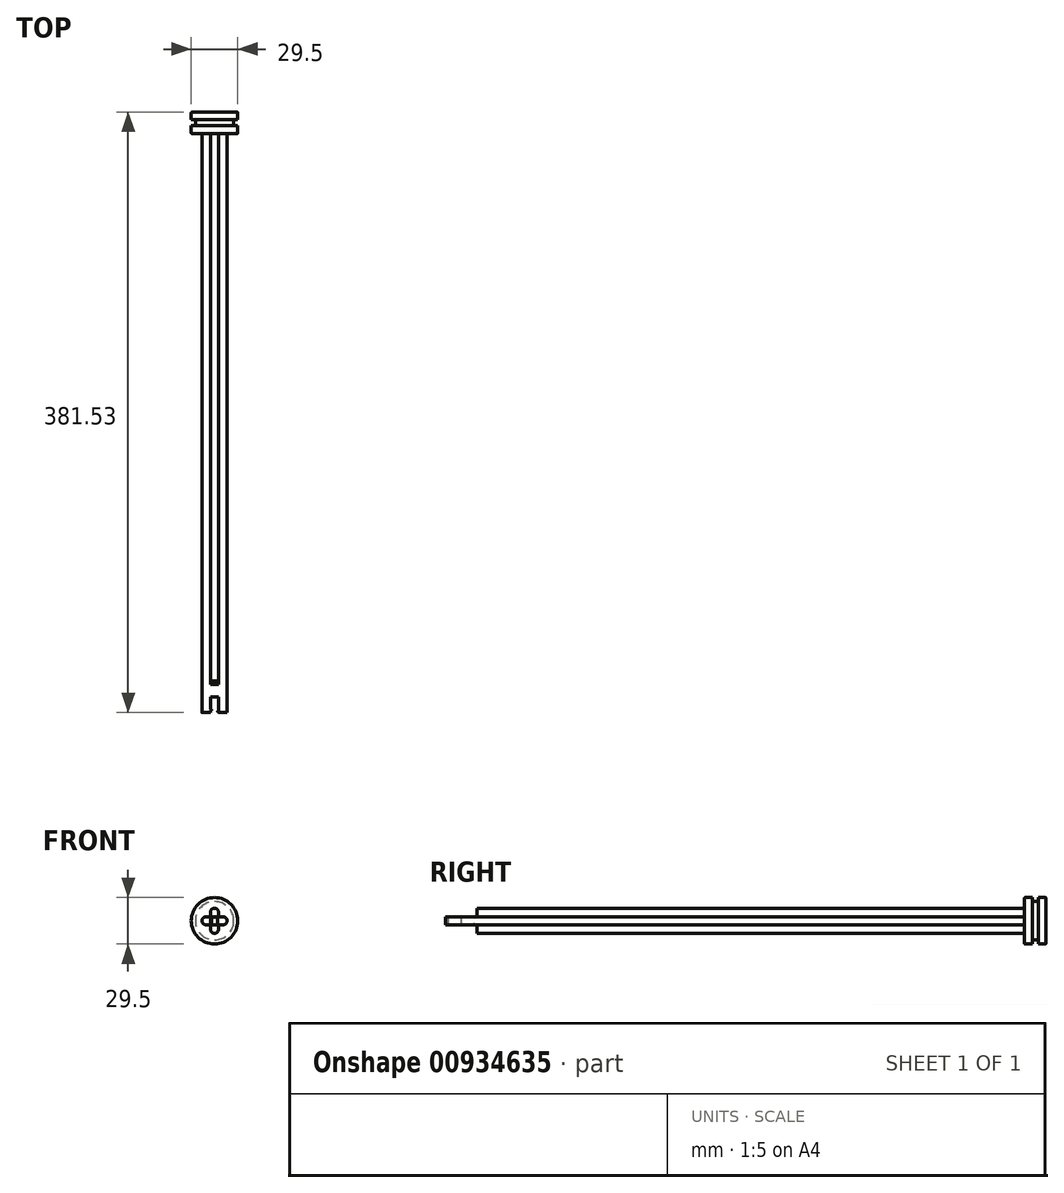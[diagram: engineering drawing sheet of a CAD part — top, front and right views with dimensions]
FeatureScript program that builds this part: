
annotation { "Feature Type Name" : "Feature", "Feature Type Description" : "" }
export const myFeature = defineFeature(function(context is Context, id is Id, definition is map)
    precondition{}
    {
        {
            var Q0;
            Q0=qCreatedBy(makeId("Front.planeOp"),FACE);
            var sketch = newSketch(context, id + "F0", { "sketchPlane" : qUnion([Q0])});
            skLineSegment(sketch, "E0.bottom", {"start": v(2.5, 8) * mm, "end": v(-2.5, 8) * mm});
            skLineSegment(sketch, "E0.top", {"start": v(2.5, -8) * mm, "end": v(-2.5, -8) * mm});
            skLineSegment(sketch, "E0.left", {"start": v(2.5, 8) * mm, "end": v(2.5, -8) * mm});
            skLineSegment(sketch, "E0.right", {"start": v(-2.5, 8) * mm, "end": v(-2.5, -8) * mm});
            skPoint(sketch, "E0.middle", {"position": v(0, 0) * mm});
            skLineSegment(sketch, "E1.bottom", {"start": v(-8, -2.5) * mm, "end": v(8, -2.5) * mm});
            skLineSegment(sketch, "E1.top", {"start": v(-8, 2.5) * mm, "end": v(8, 2.5) * mm});
            skLineSegment(sketch, "E1.left", {"start": v(-8, -2.5) * mm, "end": v(-8, 2.5) * mm});
            skLineSegment(sketch, "E1.right", {"start": v(8, -2.5) * mm, "end": v(8, 2.5) * mm});
            skSolve(sketch);
        }
        {
            var Q0;
            {var subQ5=sQuery(id+"F0.wireOp",EDGE,"E1.left");Q0=makeQuery(id+"F0.imprint","IMPRINT",FACE,{"disambiguationData":[TD([[makeQuery(id+"F0.imprint","IMPRINT",EDGE,{"derivedFrom":subQ5}),-1.0]])]});}
            var Q1;
            {var subQ0=sQuery(id+"F0.wireOp",EDGE,"E1.top");var subQ1=sQuery(id+"F0.wireOp",EDGE,"E0.left");var subQ2=makeQuery(id+"F0.imprint","INTERSECT",VERTEX,{"derivedFrom":[subQ1,subQ0]});Q1=makeQuery(id+"F0.imprint","IMPRINT",FACE,{"disambiguationData":[TD([[makeQuery(id+"F0.imprint","IMPRINT",EDGE,{"disambiguationData":[TD([[subQ2,-1.0]])],"derivedFrom":subQ1}),-1.0]])]});}
            var Q2;
            {var subQ5=sQuery(id+"F0.wireOp",EDGE,"E1.right");Q2=makeQuery(id+"F0.imprint","IMPRINT",FACE,{"disambiguationData":[TD([[makeQuery(id+"F0.imprint","IMPRINT",EDGE,{"derivedFrom":subQ5}),1.0]])]});}
            var Q3;
            {var subQ0=sQuery(id+"F0.wireOp",EDGE,"E0.top");Q3=makeQuery(id+"F0.imprint","IMPRINT",FACE,{"disambiguationData":[TD([[makeQuery(id+"F0.imprint","IMPRINT",EDGE,{"derivedFrom":subQ0}),-1.0]])]});}
            var Q4;
            {var subQ0=sQuery(id+"F0.wireOp",EDGE,"E0.bottom");Q4=makeQuery(id+"F0.imprint","IMPRINT",FACE,{"disambiguationData":[TD([[makeQuery(id+"F0.imprint","IMPRINT",EDGE,{"derivedFrom":subQ0}),1.0]])]});}
            extrude(context, id + "F1", {"entities" : qUnion([Q0, Q1, Q2, Q3, Q4]), "depth" : 367.74 * mm, "offsetDistance" : 25.4 * mm});
        }
        {
            var Q0;
            Q0=makeQuery(id+"F1.opExtrude","SWEPT_EDGE",EDGE,{"disambiguationData":[OSD([sQuery(id+"F0.wireOp",EDGE,"E0.bottom"),sQuery(id+"F0.wireOp",EDGE,"E0.right")])]});
            var Q1;
            Q1=makeQuery(id+"F1.opExtrude","SWEPT_EDGE",EDGE,{"disambiguationData":[OSD([sQuery(id+"F0.wireOp",EDGE,"E0.bottom"),sQuery(id+"F0.wireOp",EDGE,"E0.left")])]});
            var Q2;
            Q2=makeQuery(id+"F1.opExtrude","SWEPT_EDGE",EDGE,{"disambiguationData":[OSD([sQuery(id+"F0.wireOp",EDGE,"E1.top"),sQuery(id+"F0.wireOp",EDGE,"E1.left")])]});
            var Q3;
            Q3=makeQuery(id+"F1.opExtrude","SWEPT_EDGE",EDGE,{"disambiguationData":[OSD([sQuery(id+"F0.wireOp",EDGE,"E1.bottom"),sQuery(id+"F0.wireOp",EDGE,"E1.left")])]});
            var Q4;
            Q4=makeQuery(id+"F1.opExtrude","SWEPT_EDGE",EDGE,{"disambiguationData":[OSD([sQuery(id+"F0.wireOp",EDGE,"E0.top"),sQuery(id+"F0.wireOp",EDGE,"E0.right")])]});
            var Q5;
            Q5=makeQuery(id+"F1.opExtrude","SWEPT_EDGE",EDGE,{"disambiguationData":[OSD([sQuery(id+"F0.wireOp",EDGE,"E0.top"),sQuery(id+"F0.wireOp",EDGE,"E0.left")])]});
            var Q6;
            Q6=makeQuery(id+"F1.opExtrude","SWEPT_EDGE",EDGE,{"disambiguationData":[OSD([sQuery(id+"F0.wireOp",EDGE,"E1.bottom"),sQuery(id+"F0.wireOp",EDGE,"E1.right")])]});
            var Q7;
            Q7=makeQuery(id+"F1.opExtrude","SWEPT_EDGE",EDGE,{"disambiguationData":[OSD([sQuery(id+"F0.wireOp",EDGE,"E1.top"),sQuery(id+"F0.wireOp",EDGE,"E1.right")])]});
            fillet(context, id + "F2", {"entities" : qUnion([Q0, Q1, Q2, Q3, Q4, Q5, Q6, Q7]), "radius" : 2.5 * mm, "tangentPropagation" : true, "allowEdgeOverflow" : false});
        }
        {
            var Q0;
            Q0=qCreatedBy(makeId("Front.planeOp"),FACE);
            var sketch = newSketch(context, id + "F3", { "sketchPlane" : qUnion([Q0])});
            skCircle(sketch, "E2", {"center": v(0, 0) * mm, "radius": 14.75 * mm});
            skCircle(sketch, "E3", {"center": v(0, 0) * mm, "radius": 12.2 * mm});
            skSolve(sketch);
        }
        {
            var Q0;
            Q0=makeQuery(id+"F3.imprint","IMPRINT",FACE,{"disambiguationData":[TD([[makeQuery(id+"F3.imprint","IMPRINT",EDGE,{"derivedFrom":sQuery(id+"F3.wireOp",EDGE,"E2")}),1.0]])]});
            var Q1;
            Q1=makeQuery(id+"F3.imprint","IMPRINT",FACE,{"disambiguationData":[TD([[makeQuery(id+"F3.imprint","IMPRINT",EDGE,{"derivedFrom":sQuery(id+"F3.wireOp",EDGE,"E3")}),1.0]])]});
            extrude(context, id + "F4", {"entities" : qUnion([Q0, Q1]), "operationType" : NewBodyOperationType.ADD, "oppositeDirection" : true, "depth" : 13.8 * mm, "offsetDistance" : 25.4 * mm});
        }
        {
            var Q0;
            {var subQ0=sQuery(id+"F0.wireOp",EDGE,"E0.right");Q0=makeQuery(id+"F1.opExtrude","CAP_EDGE",EDGE,{"disambiguationData":[OSD([subQ0]),TDD([makeQuery(id+"F0.imprint","IMPRINT",EDGE,{"disambiguationData":[TD([[makeQuery(id+"F0.imprint","INTERSECT",VERTEX,{"derivedFrom":[sQuery(id+"F0.wireOp",EDGE,"E0.bottom"),subQ0]}),-1.0]])],"derivedFrom":subQ0})])],"isStart":true});}
            var Q1;
            Q1=makeQuery(id+"F4.opExtrude","CAP_FACE",FACE,{"disambiguationData":[OSD([sQuery(id+"F3.wireOp",EDGE,"E2")])],"isStart":true});
            var Q2;
            Q2=makeQuery(id+"F4.opExtrude","CAP_EDGE",EDGE,{"disambiguationData":[OSD([sQuery(id+"F3.wireOp",EDGE,"E2")])],"isStart":false});
            fillet(context, id + "F5", {"entities" : qUnion([Q0, Q1, Q2]), "radius" : 0.5 * mm, "tangentPropagation" : true, "allowEdgeOverflow" : false});
        }
        {
            var Q0;
            Q0=qCreatedBy(makeId("Right.planeOp"),FACE);
            var sketch = newSketch(context, id + "F6", { "sketchPlane" : qUnion([Q0])});
            skLineSegment(sketch, "E4.bottom", {"start": v(5, 22.2) * mm, "end": v(8.8, 22.2) * mm});
            skLineSegment(sketch, "E4.top", {"start": v(5, 12.2) * mm, "end": v(8.8, 12.2) * mm});
            skLineSegment(sketch, "E4.left", {"start": v(5, 22.2) * mm, "end": v(5, 12.2) * mm});
            skLineSegment(sketch, "E4.right", {"start": v(8.8, 22.2) * mm, "end": v(8.8, 12.2) * mm});
            skLineSegment(sketch, "E5", {"start": v(0, 0) * mm, "end": v(33.95, 0) * mm});
            skSolve(sketch);
        }
        {
            var Q0;
            Q0=makeQuery(id+"F6.imprint","IMPRINT",FACE,{"disambiguationData":[TD([[makeQuery(id+"F6.imprint","IMPRINT",EDGE,{"derivedFrom":sQuery(id+"F6.wireOp",EDGE,"E4.bottom")}),-1.0]])]});
            var Q1;
            Q1=sQuery(id+"F6.wireOp",EDGE,"E5");
            revolve(context, id + "F7", {"operationType" : NewBodyOperationType.REMOVE, "surfaceOperationType" : NewSurfaceOperationType.NEW, "entities" : qUnion([Q0]), "axis" : qUnion([Q1]), "revolveType" : RevolveType.FULL, "oppositeDirection" : true});
        }
        {
            var Q0;
            Q0=makeQuery(id+"F1.opExtrude","CAP_FACE",FACE,{"disambiguationData":[OSD([sQuery(id+"F0.wireOp",EDGE,"E0.bottom"),sQuery(id+"F0.wireOp",EDGE,"E0.top"),sQuery(id+"F0.wireOp",EDGE,"E0.left"),sQuery(id+"F0.wireOp",EDGE,"E0.right"),sQuery(id+"F0.wireOp",EDGE,"E1.bottom"),sQuery(id+"F0.wireOp",EDGE,"E1.top"),sQuery(id+"F0.wireOp",EDGE,"E1.left"),sQuery(id+"F0.wireOp",EDGE,"E1.right")])],"isStart":false});
            var sketch = newSketch(context, id + "F8", { "sketchPlane" : qUnion([Q0])});
            skLineSegment(sketch, "E6.bottom", {"start": v(2.5, 10) * mm, "end": v(-2.5, 10) * mm});
            skLineSegment(sketch, "E6.top", {"start": v(2.5, -10) * mm, "end": v(-2.5, -10) * mm});
            skLineSegment(sketch, "E6.left", {"start": v(2.5, 10) * mm, "end": v(2.5, -10) * mm});
            skLineSegment(sketch, "E6.right", {"start": v(-2.5, 10) * mm, "end": v(-2.5, -10) * mm});
            skPoint(sketch, "E6.middle", {"position": v(0, 0) * mm});
            skSolve(sketch);
        }
        {
            var Q0;
            {var subQ1=sQuery(id+"F0.wireOp",EDGE,"E1.top");var subQ2=sQuery(id+"F0.wireOp",EDGE,"E1.bottom");var subQ3=sQuery(id+"F0.wireOp",EDGE,"E0.right");var subQ4=sQuery(id+"F0.wireOp",EDGE,"E0.left");var subQ5=sQuery(id+"F0.wireOp",EDGE,"E0.top");var subQ6=sQuery(id+"F0.wireOp",EDGE,"E0.bottom");var subQ7=makeQuery(id+"F1.opExtrude","CAP_FACE",FACE,{"disambiguationData":[OSD([subQ6,subQ5,subQ4,subQ3,subQ2,subQ1,sQuery(id+"F0.wireOp",EDGE,"E1.left"),sQuery(id+"F0.wireOp",EDGE,"E1.right")])],"isStart":false});var subQ11=makeQuery(id+"F2.opFillet","BLEND_EDGE",EDGE,{"blendedFrom":[makeQuery(id+"F1.opExtrude","SWEPT_EDGE",EDGE,{"disambiguationData":[OSD([subQ6,subQ4])]}),subQ7],"blendedInto":[subQ7]});Q0=makeQuery(id+"F8.imprint","IMPRINT",FACE,{"disambiguationData":[TD([[makeQuery(id+"F8.imprint","IMPRINT",EDGE,{"derivedFrom":subQ11}),1.0]])]});}
            extrude(context, id + "F9", {"entities" : qUnion([Q0]), "operationType" : NewBodyOperationType.REMOVE, "oppositeDirection" : true, "depth" : 10 * mm, "offsetDistance" : 25 * mm});
        }
        {
            var Q0;
            Q0=makeQuery(id+"F9.boolean.opBoolean","COPY",FACE,{"derivedFrom":makeQuery(id+"F9.opExtrude","CAP_FACE",FACE,{"disambiguationData":[OSD([sQuery(id+"F0.wireOp",EDGE,"E0.bottom"),sQuery(id+"F0.wireOp",EDGE,"E0.top"),sQuery(id+"F0.wireOp",EDGE,"E0.left"),sQuery(id+"F0.wireOp",EDGE,"E0.right"),sQuery(id+"F0.wireOp",EDGE,"E1.bottom"),sQuery(id+"F0.wireOp",EDGE,"E1.top"),sQuery(id+"F0.wireOp",EDGE,"E1.left"),sQuery(id+"F0.wireOp",EDGE,"E1.right"),sQuery(id+"F8.wireOp",EDGE,"E6.left"),sQuery(id+"F8.wireOp",EDGE,"E6.right")])],"isStart":false})});
            var sketch = newSketch(context, id + "F10", { "sketchPlane" : qUnion([Q0])});
            skLineSegment(sketch, "E7.bottom", {"start": v(0, 8) * mm, "end": v(2.5, 8) * mm});
            skLineSegment(sketch, "E7.top", {"start": v(0, 2.5) * mm, "end": v(2.5, 2.5) * mm});
            skLineSegment(sketch, "E7.left", {"start": v(0, 8) * mm, "end": v(0, 2.5) * mm});
            skLineSegment(sketch, "E7.right", {"start": v(2.5, 8) * mm, "end": v(2.5, 2.5) * mm});
            skLineSegment(sketch, "E8.MirrorCS", {"start": v(0, 8) * mm, "end": v(-2.5, 8) * mm});
            skLineSegment(sketch, "E9.MirrorCS", {"start": v(-2.5, 8) * mm, "end": v(-2.5, 2.5) * mm});
            skLineSegment(sketch, "E10.MirrorCS", {"start": v(0, 2.5) * mm, "end": v(-2.5, 2.5) * mm});
            skLineSegment(sketch, "E11.bottom", {"start": v(-2.5, 8) * mm, "end": v(2.5, 8) * mm});
            skLineSegment(sketch, "E11.top", {"start": v(-2.5, 2.5) * mm, "end": v(2.5, 2.5) * mm});
            skLineSegment(sketch, "E12.MirrorCS", {"start": v(-2.5, -8) * mm, "end": v(-2.5, -2.5) * mm});
            skLineSegment(sketch, "E13.MirrorCS", {"start": v(-2.5, -8) * mm, "end": v(2.5, -8) * mm});
            skLineSegment(sketch, "E14.MirrorCS", {"start": v(2.5, -8) * mm, "end": v(2.5, -2.5) * mm});
            skLineSegment(sketch, "E15.MirrorCS", {"start": v(-2.5, -2.5) * mm, "end": v(2.5, -2.5) * mm});
            skSolve(sketch);
        }
        {
            var Q0;
            {var subQ15=sQuery(id+"F10.wireOp",EDGE,"E7.left");Q0=makeQuery(id+"F10.imprint","IMPRINT",FACE,{"disambiguationData":[TD([[makeQuery(id+"F10.imprint","IMPRINT",EDGE,{"derivedFrom":subQ15}),-1.0]])]});}
            var Q1;
            {var subQ13=sQuery(id+"F10.wireOp",EDGE,"E7.left");Q1=makeQuery(id+"F10.imprint","IMPRINT",FACE,{"disambiguationData":[TD([[makeQuery(id+"F10.imprint","IMPRINT",EDGE,{"derivedFrom":subQ13}),1.0]])]});}
            var Q2;
            {var subQ16=sQuery(id+"F10.wireOp",EDGE,"E15.MirrorCS");Q2=makeQuery(id+"F10.imprint","IMPRINT",FACE,{"disambiguationData":[TD([[makeQuery(id+"F10.imprint","IMPRINT",EDGE,{"derivedFrom":subQ16}),-1.0]])]});}
            extrude(context, id + "F11", {"entities" : qUnion([Q0, Q1, Q2]), "operationType" : NewBodyOperationType.REMOVE, "oppositeDirection" : true, "depth" : 10 * mm, "offsetDistance" : 25 * mm});
        }
        {
            var Q0;
            {var subQ0=sQuery(id+"F0.wireOp",EDGE,"E1.top");Q0=makeQuery(id+"F11.boolean.opBoolean","MERGE",FACE,{"derivedFrom":[makeQuery(id+"F1.opExtrude","SWEPT_FACE",FACE,{"disambiguationData":[OSD([subQ0]),TDD([makeQuery(id+"F0.imprint","IMPRINT",EDGE,{"disambiguationData":[TD([[makeQuery(id+"F0.imprint","INTERSECT",VERTEX,{"derivedFrom":[subQ0,sQuery(id+"F0.wireOp",EDGE,"E1.left")]}),-1.0]])],"derivedFrom":subQ0})])]}),makeQuery(id+"F1.opExtrude","SWEPT_FACE",FACE,{"disambiguationData":[OSD([subQ0]),TDD([makeQuery(id+"F0.imprint","IMPRINT",EDGE,{"disambiguationData":[TD([[makeQuery(id+"F0.imprint","INTERSECT",VERTEX,{"derivedFrom":[subQ0,sQuery(id+"F0.wireOp",EDGE,"E1.right")]}),1.0]])],"derivedFrom":subQ0})])]})],"fromTools":[makeQuery(id+"F11.opExtrude","SWEPT_FACE",FACE,{"disambiguationData":[OSD([sQuery(id+"F10.wireOp",EDGE,"E11.top")])]})]});}
            var sketch = newSketch(context, id + "F12", { "sketchPlane" : qUnion([Q0])});
            skLineSegment(sketch, "E16", {"start": v(2.5, -367.74) * mm, "end": v(2, -366.24) * mm});
            skLineSegment(sketch, "E17", {"start": v(2, -366.24) * mm, "end": v(2.5, -366.24) * mm});
            skLineSegment(sketch, "E18.bottom", {"start": v(2.5, -366.24) * mm, "end": v(2, -366.24) * mm});
            skLineSegment(sketch, "E18.top", {"start": v(2.5, -365.74) * mm, "end": v(2, -365.74) * mm});
            skLineSegment(sketch, "E18.left", {"start": v(2.5, -366.24) * mm, "end": v(2.5, -365.74) * mm});
            skLineSegment(sketch, "E18.right", {"start": v(2, -366.24) * mm, "end": v(2, -365.74) * mm});
            skLineSegment(sketch, "E19.bottom", {"start": v(-2.5, -367.74) * mm, "end": v(2.5, -367.74) * mm, "construction": true});
            skLineSegment(sketch, "E19.top", {"start": v(-2.5, -221.37) * mm, "end": v(2.5, -221.37) * mm, "construction": true});
            skLineSegment(sketch, "E19.left", {"start": v(-2.5, -367.74) * mm, "end": v(-2.5, -221.37) * mm, "construction": true});
            skLineSegment(sketch, "E19.right", {"start": v(2.5, -367.74) * mm, "end": v(2.5, -221.37) * mm, "construction": true});
            skLineSegment(sketch, "E20", {"start": v(0, -224.68) * mm, "end": v(0, -221.37) * mm, "construction": true});
            skPoint(sketch, "E20.startSnap0", {"position": v(0, -221.37) * mm});
            skLineSegment(sketch, "E21.MirrorCS", {"start": v(-2, -366.24) * mm, "end": v(-2.5, -366.24) * mm});
            skLineSegment(sketch, "E22.MirrorCS", {"start": v(-2.5, -366.24) * mm, "end": v(-2.5, -365.74) * mm});
            skLineSegment(sketch, "E23.MirrorCS", {"start": v(-2.5, -366.24) * mm, "end": v(-2, -366.24) * mm});
            skLineSegment(sketch, "E24.MirrorCS", {"start": v(-2, -366.24) * mm, "end": v(-2, -365.74) * mm});
            skLineSegment(sketch, "E25.MirrorCS", {"start": v(-2.5, -367.74) * mm, "end": v(-2, -366.24) * mm});
            skLineSegment(sketch, "E26.MirrorCS", {"start": v(-2.5, -365.74) * mm, "end": v(-2, -365.74) * mm});
            skSolve(sketch);
        }
        {
            var Q0;
            Q0=makeQuery(id+"F12.imprint","IMPRINT",FACE,{"disambiguationData":[TD([[makeQuery(id+"F12.imprint","IMPRINT",EDGE,{"derivedFrom":sQuery(id+"F12.wireOp",EDGE,"E22.MirrorCS")}),-1.0]])]});
            var Q1;
            {var subQ0=sQuery(id+"F12.wireOp",EDGE,"E23.MirrorCS");Q1=makeQuery(id+"F12.imprint","IMPRINT",FACE,{"disambiguationData":[TD([[makeQuery(id+"F12.imprint","IMPRINT",EDGE,{"derivedFrom":subQ0}),-1.0]])]});}
            var Q2;
            Q2=makeQuery(id+"F12.imprint","IMPRINT",FACE,{"disambiguationData":[TD([[makeQuery(id+"F12.imprint","IMPRINT",EDGE,{"derivedFrom":sQuery(id+"F12.wireOp",EDGE,"E18.bottom")}),-1.0]])]});
            var Q3;
            {var subQ0=sQuery(id+"F12.wireOp",EDGE,"E16");Q3=makeQuery(id+"F12.imprint","IMPRINT",FACE,{"disambiguationData":[TD([[makeQuery(id+"F12.imprint","IMPRINT",EDGE,{"derivedFrom":subQ0}),-1.0]])]});}
            extrude(context, id + "F13", {"entities" : qUnion([Q0, Q1, Q2, Q3]), "operationType" : NewBodyOperationType.ADD, "oppositeDirection" : true, "depth" : 5 * mm, "offsetDistance" : 25 * mm});
        }
        {
            var Q0;
            Q0=makeQuery(id+"F13.boolean.opBoolean","MERGE",EDGE,{"derivedFrom":[makeQuery(id+"F9.boolean.opBoolean","COPY",EDGE,{"derivedFrom":makeQuery(id+"F9.opExtrude","CAP_EDGE",EDGE,{"disambiguationData":[OSD([sQuery(id+"F8.wireOp",EDGE,"E6.right")])],"isStart":true})}),makeQuery(id+"F13.opExtrude","SWEPT_EDGE",EDGE,{"disambiguationData":[OSD([sQuery(id+"F0.wireOp",EDGE,"E0.right"),sQuery(id+"F0.wireOp",EDGE,"E1.top"),sQuery(id+"F12.wireOp",EDGE,"E25.MirrorCS")])]})]});
            var Q1;
            Q1=makeQuery(id+"F13.boolean.opBoolean","MERGE",EDGE,{"derivedFrom":[makeQuery(id+"F9.boolean.opBoolean","COPY",EDGE,{"derivedFrom":makeQuery(id+"F9.opExtrude","CAP_EDGE",EDGE,{"disambiguationData":[OSD([sQuery(id+"F8.wireOp",EDGE,"E6.left")])],"isStart":true})}),makeQuery(id+"F13.opExtrude","SWEPT_EDGE",EDGE,{"disambiguationData":[OSD([sQuery(id+"F0.wireOp",EDGE,"E0.left"),sQuery(id+"F0.wireOp",EDGE,"E1.top"),sQuery(id+"F12.wireOp",EDGE,"E16")])]})]});
            fillet(context, id + "F14", {"entities" : qUnion([Q0, Q1]), "radius" : .5 * mm, "tangentPropagation" : true, "allowEdgeOverflow" : false});
        }
        {
            var Q0;
            {var subQ0=sQuery(id+"F0.wireOp",EDGE,"E0.left");Q0=makeQuery(id+"F1.opExtrude","SWEPT_FACE",FACE,{"disambiguationData":[OSD([subQ0]),TDD([makeQuery(id+"F0.imprint","IMPRINT",EDGE,{"disambiguationData":[TD([[makeQuery(id+"F0.imprint","INTERSECT",VERTEX,{"derivedFrom":[sQuery(id+"F0.wireOp",EDGE,"E0.bottom"),subQ0]}),-1.0]])],"derivedFrom":subQ0})])]});}
            var sketch = newSketch(context, id + "F15", { "sketchPlane" : qUnion([Q0])});
            skLineSegment(sketch, "E27", {"start": v(-347.74, 2.5) * mm, "end": v(-347.74, -2.5) * mm, "construction": true});
            skPoint(sketch, "E28", {"position": v(-347.74, 0) * mm});
            skLineSegment(sketch, "E29", {"start": v(-347.74, 2.5) * mm, "end": v(-349.29, 2.5) * mm});
            skLineSegment(sketch, "E30", {"start": v(-349.29, 2.5) * mm, "end": v(-349.29, 2) * mm});
            skLineSegment(sketch, "E31", {"start": v(-349.29, 2) * mm, "end": v(-347.74, 2.5) * mm});
            skLineSegment(sketch, "E32.bottom", {"start": v(-349.29, 2.5) * mm, "end": v(-349.79, 2.5) * mm});
            skLineSegment(sketch, "E32.top", {"start": v(-349.29, 2) * mm, "end": v(-349.79, 2) * mm});
            skLineSegment(sketch, "E32.right", {"start": v(-349.79, 2.5) * mm, "end": v(-349.79, 2) * mm});
            skLineSegment(sketch, "E33", {"start": v(-208.07, 0) * mm, "end": v(-347.74, 0) * mm, "construction": true});
            skLineSegment(sketch, "E34.MirrorCS", {"start": v(-349.29, -2.5) * mm, "end": v(-349.29, -2) * mm});
            skLineSegment(sketch, "E35.MirrorCS", {"start": v(-349.79, -2.5) * mm, "end": v(-349.79, -2) * mm});
            skLineSegment(sketch, "E36.MirrorCS", {"start": v(-349.29, -2.5) * mm, "end": v(-349.79, -2.5) * mm});
            skLineSegment(sketch, "E37.MirrorCS", {"start": v(-349.29, -2) * mm, "end": v(-347.74, -2.5) * mm});
            skLineSegment(sketch, "E38.MirrorCS", {"start": v(-347.74, -2.5) * mm, "end": v(-349.29, -2.5) * mm});
            skLineSegment(sketch, "E39.MirrorCS", {"start": v(-349.29, -2) * mm, "end": v(-349.79, -2) * mm});
            skSolve(sketch);
        }
        {
            var Q0;
            Q0=qSketchRegion(id+"F15",true);
            extrude(context, id + "F16", {"entities" : qUnion([Q0]), "operationType" : NewBodyOperationType.REMOVE, "oppositeDirection" : true, "depth" : 5 * mm, "offsetDistance" : 25 * mm});
        }
        {
            var Q0;
            Q0=makeQuery(id+"F7.boolean.opBoolean","COPY",EDGE,{"derivedFrom":makeQuery(id+"F7.opRevolve","SWEPT_EDGE",EDGE,{"disambiguationData":[OSD([sQuery(id+"F6.wireOp",EDGE,"E4.top"),sQuery(id+"F6.wireOp",EDGE,"E4.right")])]})});
            var Q1;
            Q1=makeQuery(id+"F7.boolean.opBoolean","COPY",EDGE,{"derivedFrom":makeQuery(id+"F7.opRevolve","SWEPT_EDGE",EDGE,{"disambiguationData":[OSD([sQuery(id+"F6.wireOp",EDGE,"E4.top"),sQuery(id+"F6.wireOp",EDGE,"E4.left")])]})});
            fillet(context, id + "F17", {"entities" : qUnion([Q0, Q1]), "radius" : 1 * mm, "tangentPropagation" : true, "allowEdgeOverflow" : false});
        }
    });
